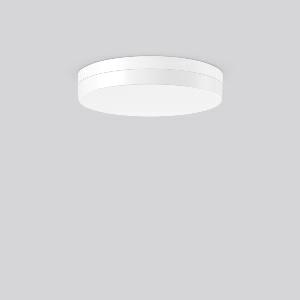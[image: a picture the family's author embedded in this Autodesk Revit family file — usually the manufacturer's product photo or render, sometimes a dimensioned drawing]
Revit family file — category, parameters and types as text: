
# Revit family: flat_slim_round_312632_002_19_151c
name_source: partatom
category: Lighting Fixtures
units: mm (PartAtom-declared; Revit-internal decimal feet)

## family parameters
Cut with Voids When Loaded = No
Host = Face
Light Source = No
Part Type = Normal
Room Calculation Point = No
Round Connector Dimension = Use Diameter
Shared = No

## types (1)
- MultiLumen 1 830 (1 x LED Modul 830, 2400 lm, 3000)
    Apparent Load = 20 VA
    CIE Flux Codes = 39 70 90 83 100
    Color Rendering = 80
    Color Temperature = 3000
    Default Elevation = 1800 mm
    Height = 70 mm
    Lamp = 1 x LED Modul 830
    Lamp Light Flux = 2400 lm
    Lamp count = 1
    Length = 400 mm
    Lifetime = 50000 h
    Luminous efficacy = 120 lm/W
    Manufacturer = RZB
    ModVariant = No
    Model = 312632.002.19
    Mounting Place = Ceiling
    Mounting Type = Surface mounted
    Number of Poles = 1
    OnlyDefault = Yes
    Power Factor = 1
    Product Name = FLAT SLIM round
    Product group = Surface mounted ceiling and wall luminaires
    ProductGroupID = 305
    Protection Class = Protection class I
    Protection Degree = Degree of protection
    RLX_Detail_Level = 1
    RLX_Emergency_Light_Flux = 0 lm
    RLX_Emergency_Type = 0
    RLX_Emergency_Type_DB = No
    RlxData = <blob elided: 20421 chars, md5=18bce1b4>
    Socket = socket
    Standby Power = 0 W
    System Light Flux = 2400 lm
    System Power = 20 W
    Type Comments = MultiLumen 1 830
    Type Image = 312631.002.jpg
    URL = http://relux.com
    VarID = multilumen_1_830
    Voltage = 0 V
    Weight = 0.00 kg
    Width = 0 mm  [stored 0 ft]

note: [stored X ft] marks values corroborated as IEEE doubles in the binary element streams (Revit-internal decimal feet)

## geometry (parser evidence)
native form markers: Blend x4, Sweep x13
no freeform markers — native parametric forms only
